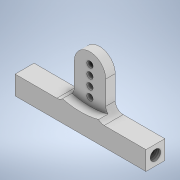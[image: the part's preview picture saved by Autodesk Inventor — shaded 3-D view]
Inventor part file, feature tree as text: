
AUTODESK INVENTOR PART (.ipt)
format: ipt  version: 2021 (Build 250183000, 183)  size: 181,760 bytes
history: native  units: mm
features: sketch x5, extrude x3, hole x2, fillet x2, projected_geometry x2
ambient origin geometry x8: Origin, YZ Plane, XZ Plane, XY Plane, X Axis, Y Axis, Z Axis, Center Point
bodies: Solid1 (feature_tree)
feature tree (14):
  extrude  "Extrusion1"  Depth=12.0mm
  hole  "Hole1"  [1 undecoded]
  hole  "Hole2"  [1 undecoded]
  extrude  "Extrusion2"  Depth=6.0mm
  fillet  "Fillet2"  Radius=6.0mm
  extrude  "Extrusion3"  Depth=10.0mm
  fillet  "Fillet4"  [1 undecoded]
  sketch  "Sketch1"  dims[d0=30.0mm d1=12.0mm]
  sketch  "Sketch2"  dims[d2=83.0mm d3=20.0mm]
  sketch  "Sketch3"  dims[d4=12.0mm d5=0.0mm d6=6.0mm]
  sketch  "Sketch4"  dims[d7=6.0mm]
  projected_geometry  "Projected Loop1"
  sketch  "Sketch5"  dims[d8=6.647mm d9=33.0mm d10=4.0mm d11=2.0mm d12=90.0deg d13=35.0mm d14=20.594885mm d15=6.0mm d16=6.0mm d17=6.647mm d18=33.0mm d19=4.0mm d20=2.0mm d21=90.0deg d22=35.0mm d23=20.594885mm d26=4.0mm d30=0.0mm d31=0.0mm d38=5.0mm d42=57.0mm d43=90.0mm d44=6.0mm d45=0.0mm d50=17.0mm d51=10.0mm d52=4.0mm d53=6.0mm d54=4.0mm d55=10.0mm d56=6.0mm d57=10.0mm d58=4.0mm d59=10.0mm d60=6.0mm d61=10.0mm d25=1.0mm d27=1.0mm d28=0.15mm d29=0.25mm d32=0.75mm d33=20.594885mm d34=0.0625mm d35=0.75mm d36=0.375mm]
  projected_geometry  "Projected Loop2"
note: 3 required parameter values undecoded (feature->parameter linkage not recoverable at this tier; creation-order binding heuristic only, values carry confidence <= 0.55)
